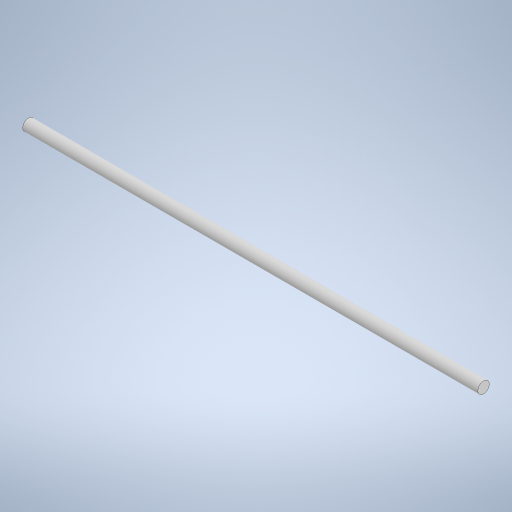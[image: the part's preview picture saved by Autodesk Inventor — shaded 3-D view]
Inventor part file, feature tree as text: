
AUTODESK INVENTOR PART (.ipt)
format: ipt  version: 2023.5 (Build 275446000, 446)  size: 218,112 bytes
history: native  units: mm
features: extrude x1, sketch x1
ambient origin geometry x8: Origin, YZ Plane, XZ Plane, XY Plane, X Axis, Y Axis, Z Axis, Center Point
bodies: 实体1 (feature_tree)
feature tree (2):
  extrude  "拉伸1"  Depth=800.0mm TaperAngle=0.0deg
  sketch  "草图1"  dims[d0=20.0mm d1=800.0mm d2=0.0mm]
